# Revit family: DAN DRYER TAPS Soaptap wall-mounted soap dispenser for liquid soap touch-less 378
name_source: partatom
category: Electrical Fixtures
revit_build: Autodesk Revit 2018 (Build: 20170223_1515(x64)
units: mm (PartAtom-declared; Revit-internal decimal feet)

## family parameters
Always vertical = Yes
Cut with Voids When Loaded = No
Host = Wall
Maintain Annotation Orientation = No
OmniClass Number = 23.80.00.00
OmniClass Title = Electric Power and Lighting
Part Type = Normal
Room Calculation Point = No
Round Connector Dimension = Use Diameter
Shared = No

## types (1)
- SoapTap Wall-mounted 378
    Airpipe = DD_White plastic
    Black = DD_Black
    Indicator = DD_Green Highlight
    Manufacturer = https://www.dandryer.com
    Model = DAN DRYER SOAPTAP WALL-MOUNTED SOAP DISPENSER FOR LIQUID SOAP TOUCH-LESS 378
    Opaque Plast = DD_White plastic
    Satin stainless steel = DD_Satin Stainless Steel
    Semi Clear plast = DD_Semiclear plastic
    URL = https://www.dandryer.com

## geometry (parser evidence)
native form markers: Sweep x6
no freeform markers — native parametric forms only
